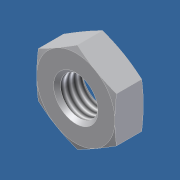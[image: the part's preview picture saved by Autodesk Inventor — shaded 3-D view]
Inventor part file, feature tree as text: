
AUTODESK INVENTOR PART (.ipt)
format: ipt  version: unknown  size: 219,648 bytes
history: native  units: in
note: dims shown in document units (in); Inventor stores cm internally (conversion verified against a paired STEP export)
features: other x70, sketch x3, revolve x2, extrude x1, thread x1
ambient origin geometry x8: Origin, YZ Plane, XZ Plane, XY Plane, X Axis, Y Axis, Z Axis, Center Point
feature tree (77):
  sketch  "Sketch_8"  dims[d0=360.0deg d1=0.16in d2=0.0in]
  sketch  "Sketch_10"  dims[d3=360.0deg d4=0.16in d5=0.0in]
  revolve  "Revolution1"  [1 undecoded]
  extrude  "Extrusion1"  Depth=0.16in TaperAngle=0.0deg
  revolve  "Revolution2"  [1 undecoded]
  thread  "Thread1"  [1 undecoded]
  other  "NUT_XY"
  other  "NUT_YZ"
  other  "NUT_ZX"
  other  "NUT_X"
  other  "NUT_Y"
  other  "NUT_Z"
  other  "NUT_Center"
  other  "a1_XY"
  other  "a1_YZ"
  other  "a1_ZX"
  other  "a1_X"
  other  "a1_Y"
  other  "a1_Z"
  other  "a1_Center"
  other  "a2_XY"
  other  "a2_YZ"
  other  "a2_ZX"
  other  "a2_X"
  other  "a2_Y"
  other  "a2_Z"
  other  "a2_Center"
  other  "b1_XY"
  other  "b1_YZ"
  other  "b1_ZX"
  other  "b1_X"
  other  "b1_Y"
  other  "b1_Z"
  other  "b1_Center"
  other  "b2_XY"
  other  "b2_YZ"
  other  "b2_ZX"
  other  "b2_X"
  other  "b2_Y"
  other  "b2_Z"
  other  "b2_Center"
  other  "e_XY"
  other  "e_YZ"
  other  "e_ZX"
  other  "e_X"
  other  "e_Y"
  other  "e_Z"
  other  "e_Center"
  other  "th1_XY"
  other  "th1_YZ"
  other  "th1_ZX"
  other  "th1_X"
  other  "th1_Y"
  other  "th1_Z"
  other  "th1_Center"
  other  "th2_XY"
  other  "th2_YZ"
  other  "th2_ZX"
  other  "th2_X"
  other  "th2_Y"
  other  "th2_Z"
  other  "th2_Center"
  other  "ol1_XY"
  other  "ol1_YZ"
  other  "ol1_ZX"
  other  "ol1_X"
  other  "ol1_Y"
  other  "ol1_Z"
  other  "ol1_Center"
  other  "ol2_XY"
  other  "ol2_YZ"
  other  "ol2_ZX"
  other  "ol2_X"
  other  "ol2_Y"
  other  "ol2_Z"
  other  "ol2_Center"
  sketch  "Sketch_11"
note: 3 required parameter values undecoded (feature->parameter linkage not recoverable at this tier; creation-order binding heuristic only, values carry confidence <= 0.55)